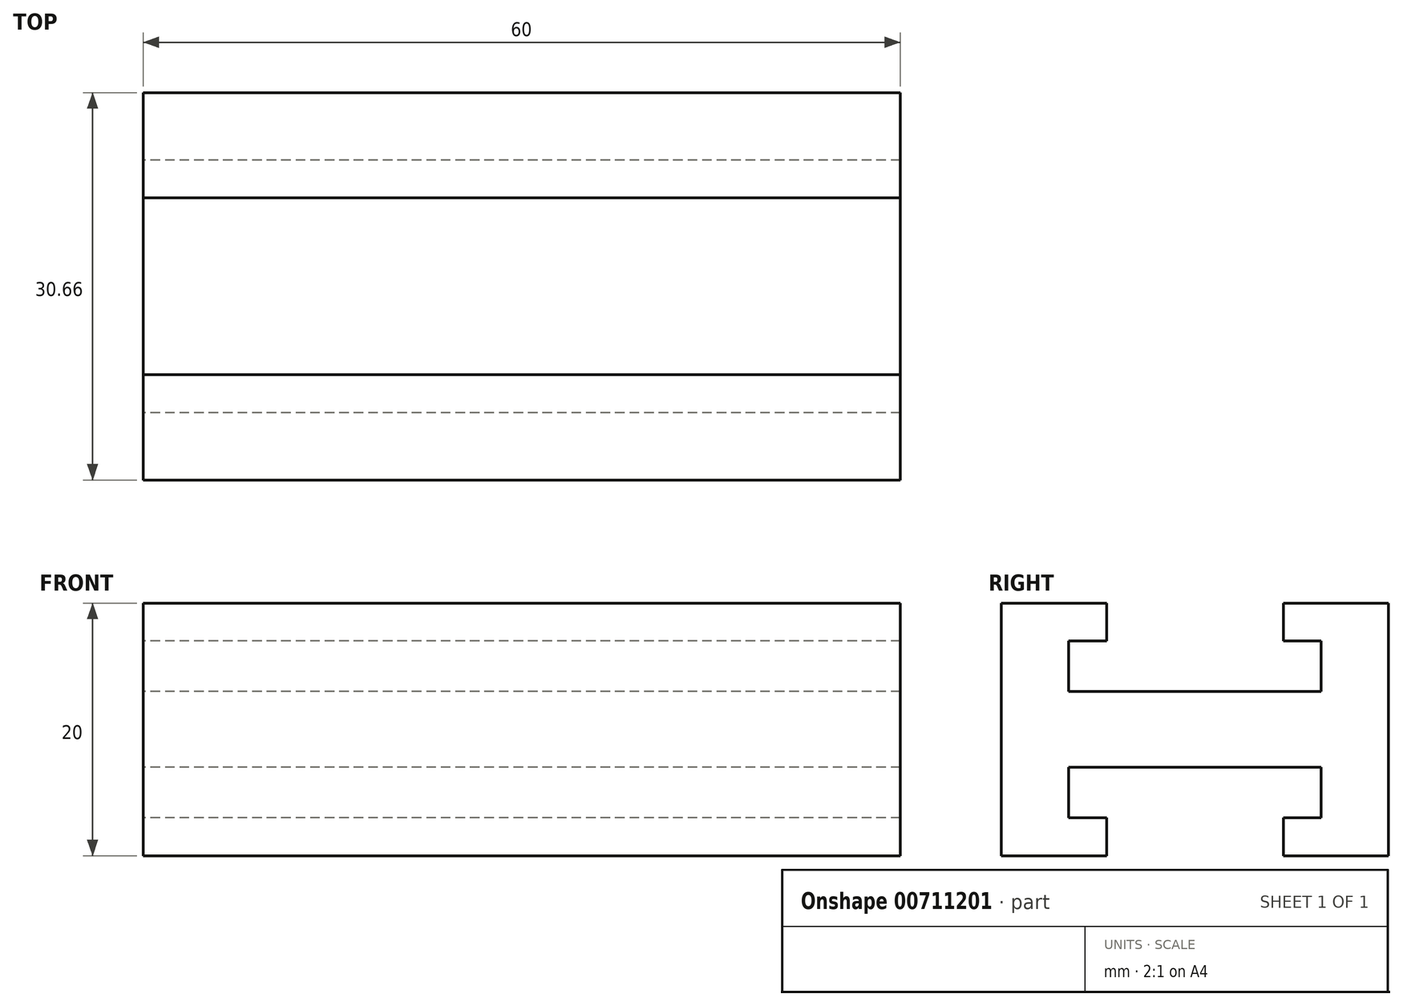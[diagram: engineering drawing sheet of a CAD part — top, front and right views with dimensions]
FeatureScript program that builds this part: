
annotation { "Feature Type Name" : "Feature", "Feature Type Description" : "" }
export const myFeature = defineFeature(function(context is Context, id is Id, definition is map)
    precondition{}
    {
        {
            var Q0;
            Q0=qCreatedBy(makeId("Right.planeOp"),FACE);
            var sketch = newSketch(context, id + "F0", { "sketchPlane" : qUnion([Q0])});
            skLineSegment(sketch, "E0.left", {"start": v(15.33, 5) * mm, "end": v(15.33, -5) * mm});
            skLineSegment(sketch, "E0.right", {"start": v(-15.33, 5) * mm, "end": v(-15.33, -5) * mm});
            skPoint(sketch, "E0.middle", {"position": v(0, 0) * mm});
            skLineSegment(sketch, "E1", {"start": v(15.33, -5) * mm, "end": v(7, -5) * mm});
            skLineSegment(sketch, "E2", {"start": v(7, -5) * mm, "end": v(7, -2) * mm});
            skLineSegment(sketch, "E3", {"start": v(7, -2) * mm, "end": v(10, -2) * mm});
            skLineSegment(sketch, "E4", {"start": v(10, -2) * mm, "end": v(10, 2) * mm});
            skLineSegment(sketch, "E5.MirrorCS", {"start": v(-10, -2) * mm, "end": v(-10, 2) * mm});
            skLineSegment(sketch, "E6.MirrorCS", {"start": v(-7, -5) * mm, "end": v(-7, -2) * mm});
            skLineSegment(sketch, "E7.MirrorCS", {"start": v(-7, -2) * mm, "end": v(-10, -2) * mm});
            skLineSegment(sketch, "E8", {"start": v(-15.33, -5) * mm, "end": v(-7, -5) * mm});
            skLineSegment(sketch, "E9", {"start": v(-10, 2) * mm, "end": v(10, 2) * mm});
            skLineSegment(sketch, "E10.left", {"start": v(-15.33, 5) * mm, "end": v(-15.33, 15) * mm});
            skLineSegment(sketch, "E10.right", {"start": v(15.33, 5) * mm, "end": v(15.33, 15) * mm});
            skPoint(sketch, "E10.middle", {"position": v(0, 10) * mm});
            skLineSegment(sketch, "E11", {"start": v(-15.33, 15) * mm, "end": v(-7, 15) * mm});
            skLineSegment(sketch, "E12", {"start": v(-7, 15) * mm, "end": v(-7, 12) * mm});
            skLineSegment(sketch, "E13", {"start": v(-7, 12) * mm, "end": v(-10, 12) * mm});
            skLineSegment(sketch, "E14", {"start": v(-10, 12) * mm, "end": v(-10, 8) * mm});
            skLineSegment(sketch, "E15.MirrorCS", {"start": v(10, 12) * mm, "end": v(10, 8) * mm});
            skLineSegment(sketch, "E16.MirrorCS", {"start": v(7, 15) * mm, "end": v(7, 12) * mm});
            skLineSegment(sketch, "E17.MirrorCS", {"start": v(7, 12) * mm, "end": v(10, 12) * mm});
            skLineSegment(sketch, "E18", {"start": v(15.33, 15) * mm, "end": v(7, 15) * mm});
            skLineSegment(sketch, "E19", {"start": v(10, 8) * mm, "end": v(-10, 8) * mm});
            skSolve(sketch);
        }
        {
            var Q0;
            Q0 = qSketchRegion(id + "F0", true);
            extrude(context, id + "F1", {"entities" : qUnion([Q0]), "depth" : 60 * mm, "offsetDistance" : 25 * mm});
        }
    });
